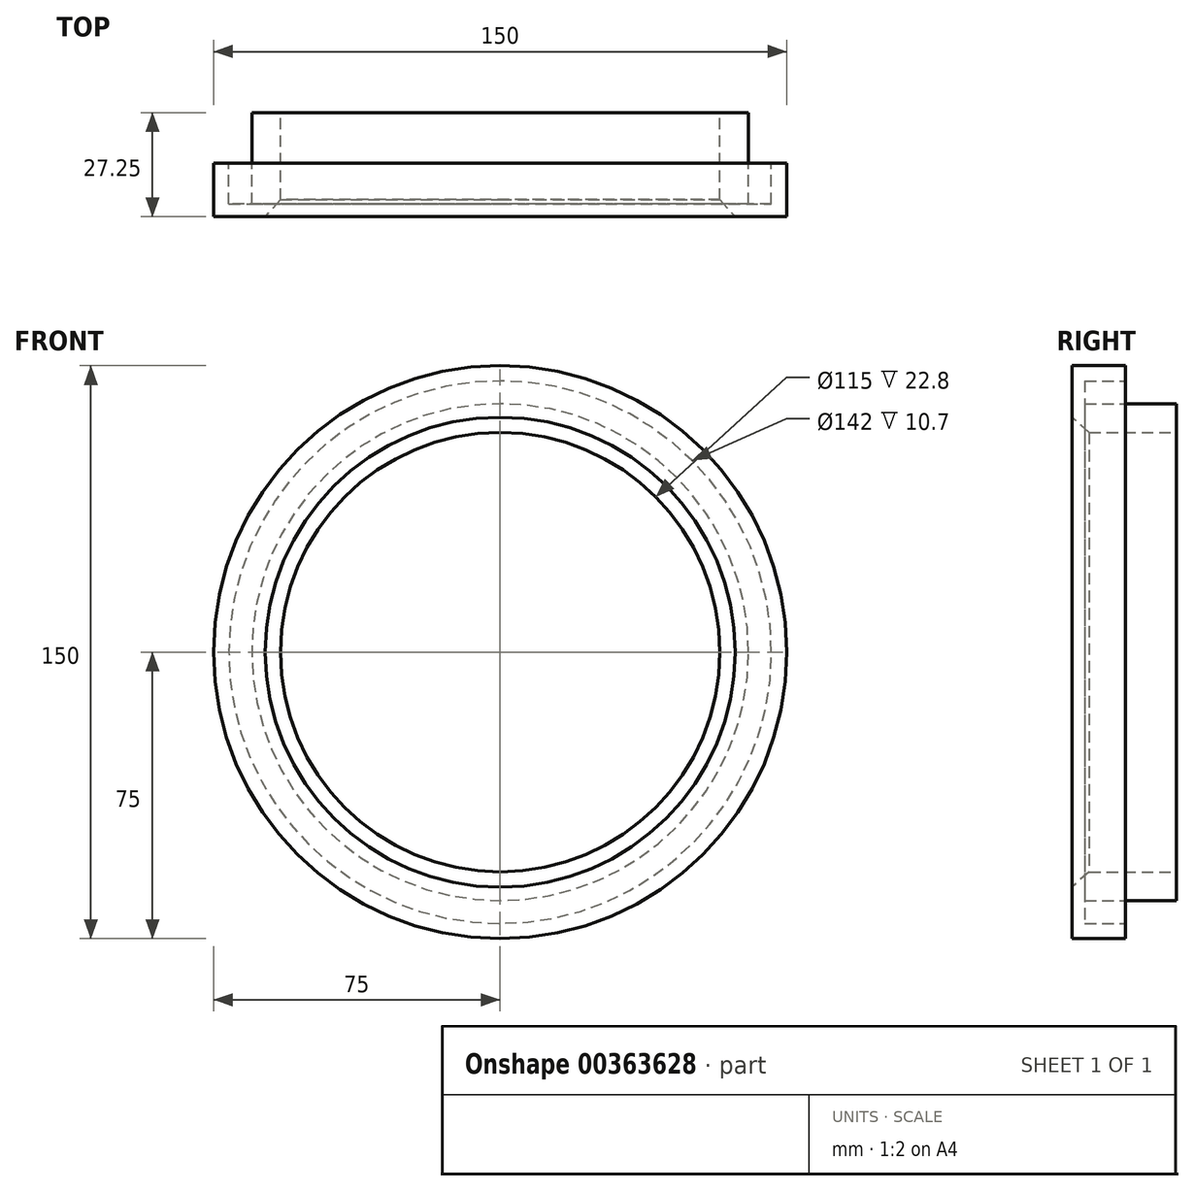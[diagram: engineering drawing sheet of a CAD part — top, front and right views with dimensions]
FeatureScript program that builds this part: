
annotation { "Feature Type Name" : "Feature", "Feature Type Description" : "" }
export const myFeature = defineFeature(function(context is Context, id is Id, definition is map)
    precondition{}
    {
        {
            var Q0;
            Q0=qCreatedBy(makeId("Right.planeOp"),FACE);
            var sketch = newSketch(context, id + "F0", { "sketchPlane" : qUnion([Q0])});
            skLineSegment(sketch, "E0", {"start": v(114.38, 0) * mm, "end": v(-95.62, 0) * mm, "construction": true});
            skLineSegment(sketch, "E1", {"start": v(27.25, 57.5) * mm, "end": v(27.25, 65) * mm});
            skLineSegment(sketch, "E2", {"start": v(27.25, 65) * mm, "end": v(3.3, 65) * mm});
            skLineSegment(sketch, "E3", {"start": v(3.3, 65) * mm, "end": v(3.3, 71) * mm});
            skLineSegment(sketch, "E4", {"start": v(3.3, 71) * mm, "end": v(14, 71) * mm});
            skLineSegment(sketch, "E5", {"start": v(14, 71) * mm, "end": v(14, 75) * mm});
            skLineSegment(sketch, "E6", {"start": v(14, 75) * mm, "end": v(0, 75) * mm});
            skLineSegment(sketch, "E7", {"start": v(27.25, 57.5) * mm, "end": v(4.45, 57.5) * mm});
            skLineSegment(sketch, "E8", {"start": v(4.45, 57.5) * mm, "end": v(0, 61.5) * mm});
            skLineSegment(sketch, "E9", {"start": v(0, 61.5) * mm, "end": v(0, 75) * mm});
            skSolve(sketch);
        }
        {
            var Q0;
            Q0 = qSketchRegion(id + "F0", true);
            var Q1;
            Q1=sQuery(id+"F0.wireOp",EDGE,"E0");
            revolve(context, id + "F1", {"entities" : qUnion([Q0]), "axis" : qUnion([Q1]), "revolveType" : RevolveType.FULL});
        }
    });
